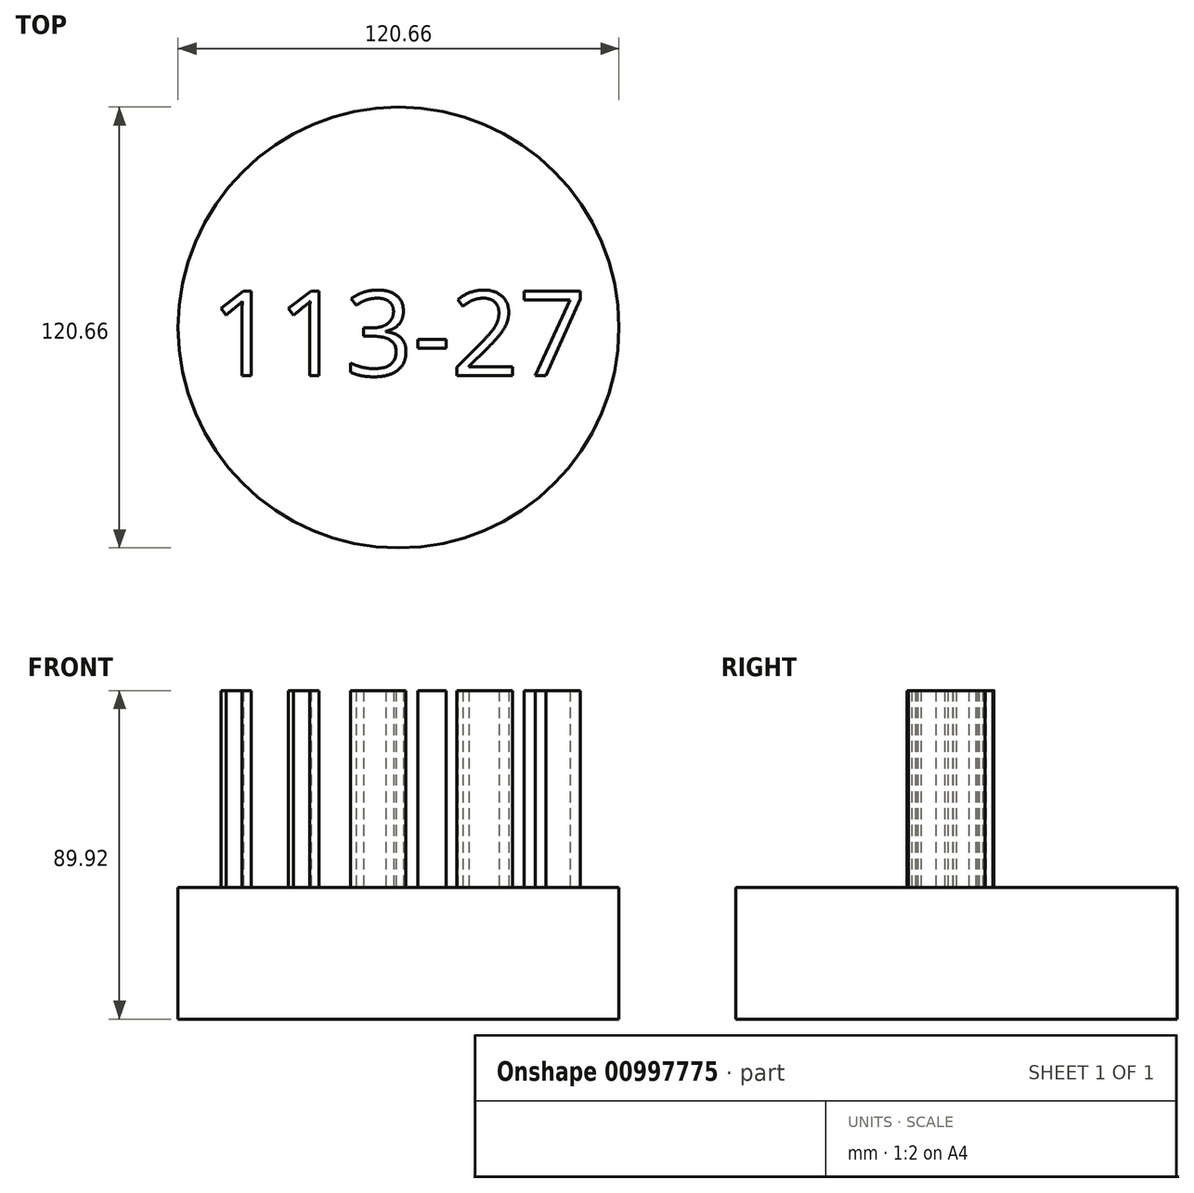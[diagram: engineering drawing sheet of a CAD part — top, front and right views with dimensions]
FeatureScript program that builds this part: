
annotation { "Feature Type Name" : "Feature", "Feature Type Description" : "" }
export const myFeature = defineFeature(function(context is Context, id is Id, definition is map)
    precondition{}
    {
        {
            var Q0;
            Q0=qCreatedBy(makeId("Top.planeOp"),FACE);
            var sketch = newSketch(context, id + "F0", { "sketchPlane" : qUnion([Q0])});
            skCircle(sketch, "E0", {"center": v(0, 0) * mm, "radius": 60.33 * mm});
            skSolve(sketch);
        }
        {
            var Q0;
            Q0 = qSketchRegion(id + "F0", true);
            extrude(context, id + "F1", {"entities" : qUnion([Q0]), "depth" : 36.07 * mm, "offsetDistance" : 25.4 * mm});
        }
        {
            var Q0;
            Q0=makeQuery(id+"F1.opExtrude","CAP_FACE",FACE,{"disambiguationData":[OSD([sQuery(id+"F0.wireOp",EDGE,"E0")])],"isStart":false});
            var sketch = newSketch(context, id + "F2", { "sketchPlane" : qUnion([Q0])});
            skText(sketch, "E1", { "text": "113-27", "fontName": "OpenSans-Regular.ttf"});
            const initialGuessF2  = {"E1": [-0.05159, -0.01317, 1, 0, 0.02331]};
            skSetInitialGuess(sketch, initialGuessF2);
            skSolve(sketch);
        }
        {
            var Q0;
            Q0 = qSketchRegion(id + "F2", true);
            extrude(context, id + "F3", {"entities" : qUnion([Q0]), "operationType" : NewBodyOperationType.ADD, "depth" : 53.85 * mm, "offsetDistance" : 25.4 * mm});
        }
    });
